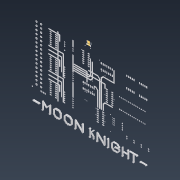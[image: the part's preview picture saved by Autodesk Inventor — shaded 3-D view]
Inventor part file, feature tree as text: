
AUTODESK INVENTOR PART (.ipt)
format: ipt  version: 2022.3 (Build 263350000, 350)  size: 4,913,664 bytes
history: mixed  units: in
note: dims shown in document units (in); Inventor stores cm internally (conversion verified against a paired STEP export)
features: other x297, projected_geometry x12, extrude x1, fillet x1, sketch x1, imported_body x1
ambient origin geometry x8: Origin, YZ Plane, XZ Plane, XY Plane, X Axis, Y Axis, Z Axis, Center Point
bodies: Solid1 (imported_parasolid), Solid2 (imported_parasolid), Solid3 (imported_parasolid), Solid4 (imported_parasolid), Solid5 (imported_parasolid), Solid6 (imported_parasolid), Solid7 (imported_parasolid), Solid8 (imported_parasolid), Solid9 (imported_parasolid), Solid10 (imported_parasolid), Solid11 (imported_parasolid), Solid12 (imported_parasolid), Solid13 (imported_parasolid), Solid14 (imported_parasolid), Solid15 (imported_parasolid), Solid16 (imported_parasolid), Solid17 (imported_parasolid), Solid18 (imported_parasolid), Solid19 (imported_parasolid), Solid20 (imported_parasolid), Solid21 (imported_parasolid), Solid22 (imported_parasolid), Solid23 (imported_parasolid), Solid24 (imported_parasolid), Solid25 (imported_parasolid), Solid26 (imported_parasolid), Solid27 (imported_parasolid), Solid28 (imported_parasolid), Solid29 (imported_parasolid), Solid30 (imported_parasolid), Solid31 (imported_parasolid), Solid32 (imported_parasolid), Solid33 (imported_parasolid), Solid34 (imported_parasolid), Solid35 (imported_parasolid), Solid36 (imported_parasolid), Solid37 (imported_parasolid), Solid38 (imported_parasolid), Solid39 (imported_parasolid), Solid40 (imported_parasolid), Solid41 (imported_parasolid), Solid42 (imported_parasolid), Solid43 (imported_parasolid), Solid44 (imported_parasolid), Solid45 (imported_parasolid), Solid46 (imported_parasolid), Solid47 (imported_parasolid), Solid48 (imported_parasolid), Solid49 (imported_parasolid), Solid50 (imported_parasolid), Solid51 (imported_parasolid), Solid52 (imported_parasolid), Solid53 (imported_parasolid), Solid54 (imported_parasolid), Solid55 (imported_parasolid), Solid56 (imported_parasolid), Solid57 (imported_parasolid), Solid58 (imported_parasolid), Solid59 (imported_parasolid), Solid60 (imported_parasolid), Solid61 (imported_parasolid), Solid62 (imported_parasolid), Solid63 (imported_parasolid), Solid64 (imported_parasolid), Solid65 (imported_parasolid), Solid66 (imported_parasolid), Solid67 (imported_parasolid), Solid68 (imported_parasolid), Solid69 (imported_parasolid), Solid70 (imported_parasolid), Solid71 (imported_parasolid), Solid72 (imported_parasolid), Solid73 (imported_parasolid), Solid74 (imported_parasolid), Solid75 (imported_parasolid), Solid76 (imported_parasolid), Solid77 (imported_parasolid), Solid78 (imported_parasolid), Solid79 (imported_parasolid), Solid80 (imported_parasolid), Solid81 (imported_parasolid), Solid82 (imported_parasolid), Solid83 (imported_parasolid), Solid84 (imported_parasolid), Solid85 (imported_parasolid), Solid86 (imported_parasolid), Solid87 (imported_parasolid), Solid88 (imported_parasolid), Solid89 (imported_parasolid), Solid90 (imported_parasolid), Solid91 (imported_parasolid), Solid92 (imported_parasolid), Solid93 (imported_parasolid), Solid94 (imported_parasolid), Solid95 (imported_parasolid), Solid96 (imported_parasolid), Solid97 (imported_parasolid), Solid98 (imported_parasolid), Solid99 (imported_parasolid), Solid100 (imported_parasolid), Solid101 (imported_parasolid), Solid102 (imported_parasolid), Solid103 (imported_parasolid), Solid104 (imported_parasolid), Solid105 (imported_parasolid), Solid106 (imported_parasolid), Solid107 (imported_parasolid), Solid108 (imported_parasolid), Solid109 (imported_parasolid), Solid110 (imported_parasolid), Solid111 (imported_parasolid), Solid112 (imported_parasolid), Solid113 (imported_parasolid), Solid114 (imported_parasolid), Solid115 (imported_parasolid), Solid116 (imported_parasolid), Solid117 (imported_parasolid), Solid118 (imported_parasolid), Solid119 (imported_parasolid), Solid120 (imported_parasolid), Solid121 (imported_parasolid), Solid122 (imported_parasolid), Solid123 (imported_parasolid), Solid124 (imported_parasolid), Solid125 (imported_parasolid), Solid126 (imported_parasolid), Solid127 (imported_parasolid), Solid128 (imported_parasolid), Solid129 (imported_parasolid), Solid130 (imported_parasolid), Solid131 (imported_parasolid), Solid132 (imported_parasolid), Solid133 (imported_parasolid), Solid134 (imported_parasolid), Solid135 (imported_parasolid), Solid136 (imported_parasolid), Solid137 (imported_parasolid), Solid138 (imported_parasolid), Solid139 (imported_parasolid), Solid140 (imported_parasolid), Solid141 (imported_parasolid), Solid142 (imported_parasolid), Solid143 (imported_parasolid), Solid144 (imported_parasolid), Solid145 (imported_parasolid), Solid146 (imported_parasolid), Solid147 (imported_parasolid), Solid148 (imported_parasolid), Solid149 (imported_parasolid), Solid150 (imported_parasolid), Solid151 (imported_parasolid), Solid152 (imported_parasolid), Solid153 (imported_parasolid), Solid154 (imported_parasolid), Solid155 (imported_parasolid), Solid156 (imported_parasolid), Solid157 (imported_parasolid), Solid158 (imported_parasolid), Solid159 (imported_parasolid), Solid160 (imported_parasolid), Solid161 (imported_parasolid), Solid162 (imported_parasolid), Solid163 (imported_parasolid), Solid164 (imported_parasolid), Solid165 (imported_parasolid), Solid166 (imported_parasolid), Solid167 (imported_parasolid), Solid168 (imported_parasolid), Solid169 (imported_parasolid), Solid170 (imported_parasolid), Solid171 (imported_parasolid), Solid172 (imported_parasolid), Solid173 (imported_parasolid), Solid174 (imported_parasolid), Solid175 (imported_parasolid), Solid176 (imported_parasolid), Solid177 (imported_parasolid), Solid178 (imported_parasolid), Solid179 (imported_parasolid), Solid180 (imported_parasolid), Solid181 (imported_parasolid), Solid182 (imported_parasolid), Solid183 (imported_parasolid), Solid184 (imported_parasolid), Solid185 (imported_parasolid), Solid186 (imported_parasolid), Solid187 (imported_parasolid), Solid188 (imported_parasolid), Solid189 (imported_parasolid), Solid190 (imported_parasolid), Solid191 (imported_parasolid), Solid192 (imported_parasolid), Solid193 (imported_parasolid), Solid194 (imported_parasolid), Solid195 (imported_parasolid), Solid196 (imported_parasolid), Solid197 (imported_parasolid), Solid198 (imported_parasolid), Solid199 (imported_parasolid), Solid200 (imported_parasolid), Solid201 (imported_parasolid), Solid202 (imported_parasolid), Solid203 (imported_parasolid), Solid204 (imported_parasolid), Solid205 (imported_parasolid), Solid206 (imported_parasolid), Solid207 (imported_parasolid), Solid208 (imported_parasolid), Solid209 (imported_parasolid), Solid210 (imported_parasolid), Solid211 (imported_parasolid), Solid212 (imported_parasolid), Solid213 (imported_parasolid), Solid214 (imported_parasolid), Solid215 (imported_parasolid), Solid216 (imported_parasolid), Solid217 (imported_parasolid), Solid218 (imported_parasolid), Solid219 (imported_parasolid), Solid220 (imported_parasolid), Solid221 (imported_parasolid), Solid222 (imported_parasolid), Solid223 (imported_parasolid), Solid224 (imported_parasolid), Solid225 (imported_parasolid), Solid226 (imported_parasolid), Solid227 (imported_parasolid), Solid228 (imported_parasolid), Solid229 (imported_parasolid), Solid230 (imported_parasolid), Solid231 (imported_parasolid), Solid232 (imported_parasolid), Solid233 (imported_parasolid), Solid234 (imported_parasolid), Solid235 (imported_parasolid), Solid236 (imported_parasolid), Solid237 (imported_parasolid), Solid238 (imported_parasolid), Solid239 (imported_parasolid), Solid240 (imported_parasolid), Solid241 (imported_parasolid), Solid242 (imported_parasolid), Solid243 (imported_parasolid), Solid244 (imported_parasolid), Solid245 (imported_parasolid), Solid246 (imported_parasolid), Solid247 (imported_parasolid), Solid248 (imported_parasolid), Solid249 (imported_parasolid), Solid250 (imported_parasolid), Solid251 (imported_parasolid), Solid252 (imported_parasolid), Solid253 (imported_parasolid), Solid254 (imported_parasolid), Solid255 (imported_parasolid), Solid256 (imported_parasolid), Solid257 (imported_parasolid), Solid258 (imported_parasolid), Solid259 (imported_parasolid), Solid260 (imported_parasolid), Solid261 (imported_parasolid), Solid262 (imported_parasolid), Solid263 (imported_parasolid), Solid264 (imported_parasolid), Solid265 (imported_parasolid), Solid266 (imported_parasolid), Solid267 (imported_parasolid), Solid268 (imported_parasolid), Solid269 (imported_parasolid), Solid270 (imported_parasolid), Solid271 (imported_parasolid), Solid272 (imported_parasolid), Solid273 (imported_parasolid), Solid274 (imported_parasolid), Solid275 (imported_parasolid), Solid276 (imported_parasolid), Solid277 (imported_parasolid), Solid278 (imported_parasolid), Solid279 (imported_parasolid), Solid280 (imported_parasolid), Solid281 (imported_parasolid), Solid282 (imported_parasolid), Solid283 (imported_parasolid), Solid284 (imported_parasolid), Solid285 (imported_parasolid), Solid286 (imported_parasolid), Solid287 (imported_parasolid), Solid288 (imported_parasolid), Solid289 (imported_parasolid), Solid290 (imported_parasolid), Solid291 (imported_parasolid), Solid292 (imported_parasolid), Solid293 (imported_parasolid), Solid294 (imported_parasolid), Solid295 (imported_parasolid), Solid296 (imported_parasolid), Solid297 (imported_parasolid), Solid298 (imported_parasolid), Solid299 (imported_parasolid), Body1 (imported_parasolid), Body3 (imported_parasolid)
feature tree (313):
  extrude  "Extrusion1"  Depth=0.0197in
  fillet  "Fillet1"  [1 undecoded]
  sketch  "Sketch1"  dims[d0=0.0591in d1=0.0in d2=0.0197in d3=0.0in d4=0.0in d5=0.0in d6=0.0in]
  projected_geometry  "Projected Loop1"
  projected_geometry  "Projected Loop2"
  projected_geometry  "Projected Loop3"
  projected_geometry  "Projected Loop4"
  projected_geometry  "Projected Loop5"
  projected_geometry  "Projected Loop6"
  projected_geometry  "Projected Loop7"
  projected_geometry  "Projected Loop8"
  projected_geometry  "Projected Loop9"
  projected_geometry  "Projected Loop10"
  projected_geometry  "Projected Loop11"
  projected_geometry  "Projected Loop12"
  other  "Body1:1"
  other  "Body1:2"
  other  "Body1:3"
  other  "Body1:4"
  other  "Body1:5"
  other  "Body1:6"
  other  "Body1:7"
  other  "Body1:8"
  other  "Body1:9"
  other  "Body1:10"
  other  "Body1:11"
  other  "Body1:12"
  other  "Body1:13"
  other  "Body1:14"
  other  "Body1:15"
  other  "Body1:16"
  other  "Body1:17"
  other  "Body1:18"
  other  "Body1:19"
  other  "Body1:20"
  other  "Body1:21"
  other  "Body1:22"
  other  "Body1:23"
  other  "Body1:24"
  other  "Body1:25"
  other  "Body1:26"
  other  "Body1:27"
  other  "Body1:28"
  other  "Body1:29"
  other  "Body1:30"
  other  "Body1:31"
  other  "Body1:32"
  other  "Body1:33"
  other  "Body1:34"
  other  "Body1:35"
  other  "Body1:36"
  other  "Body1:37"
  other  "Body1:38"
  other  "Body1:39"
  other  "Body1:40"
  other  "Body1:41"
  other  "Body1:42"
  other  "Body1:43"
  other  "Body1:44"
  other  "Body1:45"
  other  "Body1:46"
  other  "Body1:47"
  other  "Body1:48"
  other  "Body1:49"
  other  "Body1:50"
  other  "Body1:51"
  other  "Body1:52"
  other  "Body1:53"
  other  "Body1:54"
  other  "Body1:55"
  other  "Body1:56"
  other  "Body1:57"
  other  "Body1:58"
  other  "Body1:59"
  other  "Body1:60"
  other  "Body1:61"
  other  "Body1:62"
  other  "Body1:63"
  other  "Body1:64"
  other  "Body1:65"
  other  "Body1:66"
  other  "Body1:67"
  other  "Body1:68"
  other  "Body1:69"
  other  "Body1:70"
  other  "Body1:71"
  other  "Body1:72"
  other  "Body1:73"
  other  "Body1:74"
  other  "Body1:75"
  other  "Body1:76"
  other  "Body1:77"
  other  "Body1:78"
  other  "Body1:79"
  other  "Body1:80"
  other  "Body1:81"
  other  "Body1:82"
  other  "Body1:83"
  other  "Body1:84"
  other  "Body1:85"
  other  "Body1:86"
  other  "Body1:87"
  other  "Body1:88"
  other  "Body1:89"
  other  "Body1:90"
  other  "Body1:91"
  other  "Body1:92"
  other  "Body1:93"
  other  "Body1:94"
  other  "Body1:95"
  other  "Body1:96"
  other  "Body1:97"
  other  "Body1:98"
  other  "Body1:99"
  other  "Body1:100"
  other  "Body1:101"
  other  "Body1:102"
  other  "Body1:103"
  other  "Body1:104"
  other  "Body1:105"
  other  "Body1:106"
  other  "Body1:107"
  other  "Body1:108"
  other  "Body1:109"
  other  "Body1:110"
  other  "Body1:111"
  other  "Body1:112"
  other  "Body1:113"
  other  "Body1:114"
  other  "Body1:115"
  other  "Body1:116"
  other  "Body1:117"
  other  "Body1:118"
  other  "Body1:119"
  other  "Body1:120"
  other  "Body1:121"
  other  "Body1:122"
  other  "Body1:123"
  other  "Body1:124"
  other  "Body1:125"
  other  "Body1:126"
  other  "Body1:127"
  other  "Body1:128"
  other  "Body1:129"
  other  "Body1:130"
  other  "Body1:131"
  other  "Body1:132"
  other  "Body1:133"
  other  "Body1:134"
  other  "Body1:135"
  other  "Body1:136"
  other  "Body1:137"
  other  "Body1:138"
  other  "Body1:139"
  other  "Body1:140"
  other  "Body1:141"
  other  "Body1:142"
  other  "Body1:143"
  other  "Body1:144"
  other  "Body1:145"
  other  "Body1:146"
  other  "Body1:147"
  other  "Body1:148"
  other  "Body1:149"
  other  "Body1:150"
  other  "Body1:151"
  other  "Body1:152"
  other  "Body1:153"
  other  "Body1:154"
  other  "Body1:155"
  other  "Body1:156"
  other  "Body1:157"
  other  "Body1:158"
  other  "Body1:159"
  other  "Body1:160"
  other  "Body1:161"
  other  "Body1:162"
  other  "Body1:163"
  other  "Body1:164"
  other  "Body1:165"
  other  "Body1:166"
  other  "Body1:167"
  other  "Body1:168"
  other  "Body1:169"
  other  "Body1:170"
  other  "Body1:171"
  other  "Body1:172"
  other  "Body1:173"
  other  "Body1:174"
  other  "Body1:175"
  other  "Body1:176"
  other  "Body1:177"
  other  "Body1:178"
  other  "Body1:179"
  other  "Body1:180"
  other  "Body1:181"
  other  "Body1:182"
  other  "Body1:183"
  other  "Body1:184"
  other  "Body1:185"
  other  "Body1:186"
  other  "Body1:187"
  other  "Body1:188"
  other  "Body1:189"
  other  "Body1:190"
  other  "Body1:191"
  other  "Body1:192"
  other  "Body1:193"
  other  "Body1:194"
  other  "Body1:195"
  other  "Body1:196"
  other  "Body1:197"
  other  "Body1:198"
  other  "Body1:199"
  other  "Body1:200"
  other  "Body1:201"
  other  "Body1:202"
  other  "Body1:203"
  other  "Body1:204"
  other  "Body1:205"
  other  "Body1:206"
  other  "Body1:207"
  other  "Body1:208"
  other  "Body1:209"
  other  "Body1:210"
  other  "Body1:211"
  other  "Body1:212"
  other  "Body1:213"
  other  "Body1:214"
  other  "Body1:215"
  other  "Body1:216"
  other  "Body1:217"
  other  "Body1:218"
  other  "Body1:219"
  other  "Body1:220"
  other  "Body1:221"
  other  "Body1:222"
  other  "Body1:223"
  other  "Body1:224"
  other  "Body1:225"
  other  "Body1:226"
  other  "Body1:227"
  other  "Body1:228"
  other  "Body1:229"
  other  "Body1:230"
  other  "Body1:231"
  other  "Body1:232"
  other  "Body1:233"
  other  "Body1:234"
  other  "Body1:235"
  other  "Body1:236"
  other  "Body1:237"
  other  "Body1:238"
  other  "Body1:239"
  other  "Body1:240"
  other  "Body1:241"
  other  "Body1:242"
  other  "Body1:243"
  other  "Body1:244"
  other  "Body1:245"
  other  "Body1:246"
  other  "Body1:247"
  other  "Body1:248"
  other  "Body1:249"
  other  "Body1:250"
  other  "Body1:251"
  other  "Body1:252"
  other  "Body1:253"
  other  "Body1:254"
  other  "Body1:255"
  other  "Body1:256"
  other  "Body1:257"
  other  "Body1:258"
  other  "Body1:259"
  other  "Body1:260"
  other  "Body1:261"
  other  "Body1:262"
  other  "Body1:263"
  other  "Body1:264"
  other  "Body1:265"
  other  "Body1:266"
  other  "Body1:267"
  other  "Body1:268"
  other  "Body1:269"
  other  "Body1:270"
  other  "Body1:271"
  other  "Body1:272"
  other  "Body1:273"
  other  "Body1:274"
  other  "Body1:275"
  other  "Body1:276"
  other  "Body1:277"
  other  "Body1:278"
  other  "Body1:279"
  other  "Body1:280"
  other  "Body1:281"
  other  "Body1:282"
  other  "Body1:283"
  other  "Body1:284"
  other  "Body1:285"
  other  "Body1:286"
  other  "Body1:287"
  other  "Body1:288"
  other  "Body1:289"
  other  "Body1:290"
  other  "Body1:291"
  other  "Body1:292"
  other  "Body1:293"
  other  "Body1:294"
  other  "Body1:295"
  other  "Body1:296"
  other  "Body1:297"
  imported_body  NMx_Import_Brep_tag  [imported B-rep: ~2135 faces, bbox_mm=[163.09413, 115.165, 1.535]]
note: 1 required parameter value undecoded (feature->parameter linkage not recoverable at this tier; creation-order binding heuristic only, values carry confidence <= 0.55)
